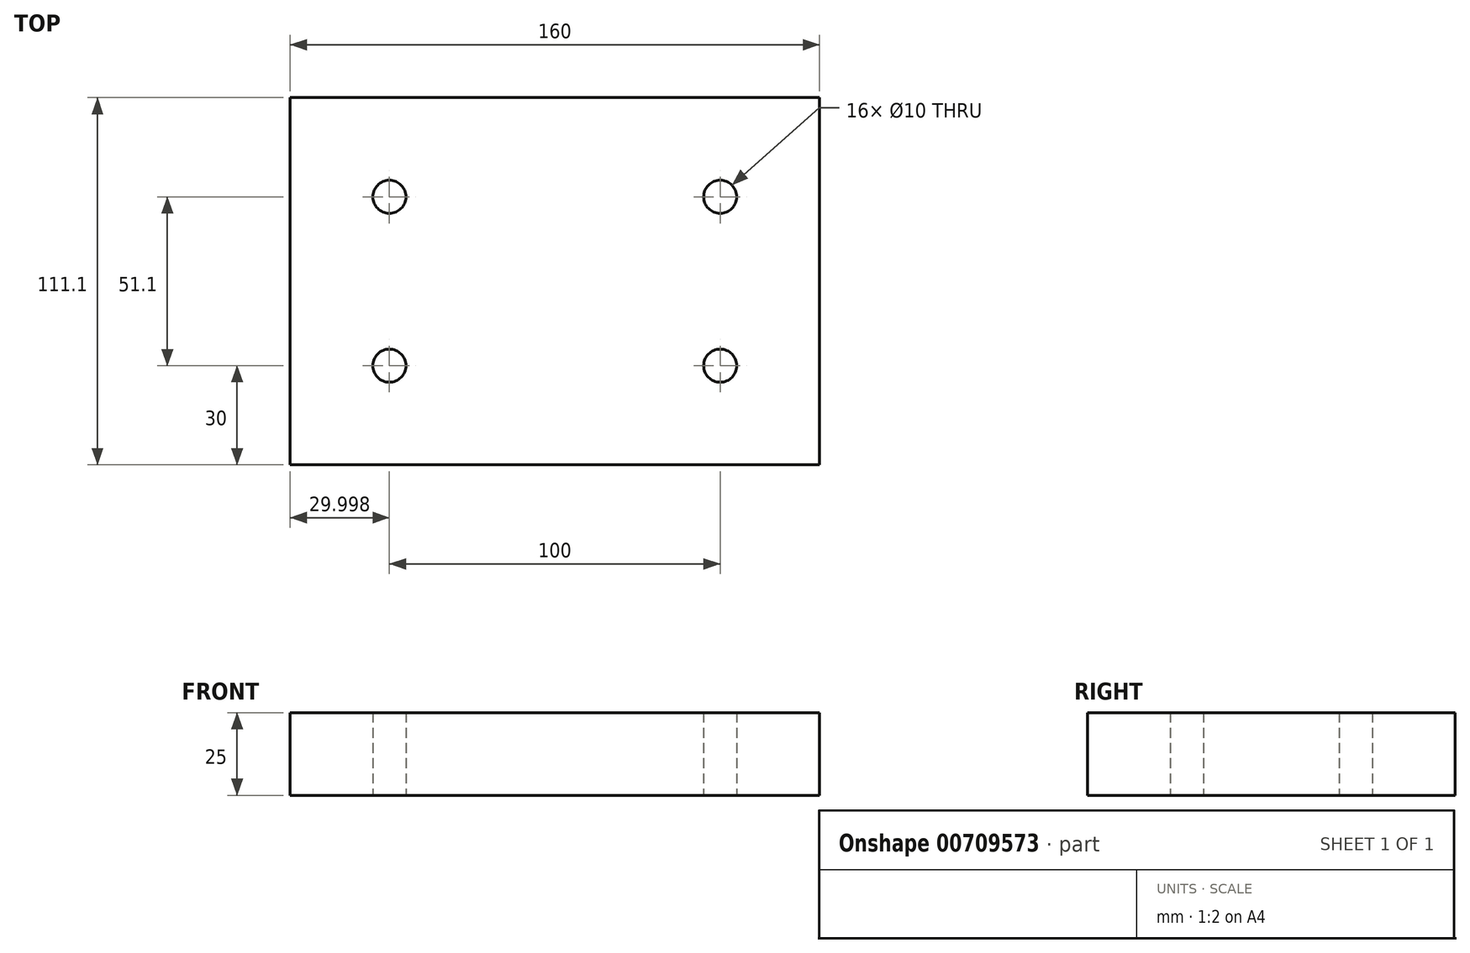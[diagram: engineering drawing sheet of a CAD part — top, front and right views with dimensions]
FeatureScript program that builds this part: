
annotation { "Feature Type Name" : "Feature", "Feature Type Description" : "" }
export const myFeature = defineFeature(function(context is Context, id is Id, definition is map)
    precondition{}
    {
        {
            var Q0;
            Q0=qCreatedBy(makeId("Top.planeOp"),FACE);
            var sketch = newSketch(context, id + "F0", { "sketchPlane" : qUnion([Q0])});
            skLineSegment(sketch, "E0.bottom", {"start": v(-87, 81.1) * mm, "end": v(73, 81.1) * mm});
            skLineSegment(sketch, "E0.top", {"start": v(-87, -30) * mm, "end": v(73, -30) * mm});
            skLineSegment(sketch, "E0.left", {"start": v(-87, 81.1) * mm, "end": v(-87, -30) * mm});
            skLineSegment(sketch, "E0.right", {"start": v(73, 81.1) * mm, "end": v(73, -30) * mm});
            skCircle(sketch, "E1", {"center": v(-57, 51.1) * mm, "radius": 5 * mm});
            skCircle(sketch, "E2", {"center": v(-57, 0) * mm, "radius": 5 * mm});
            skCircle(sketch, "E3", {"center": v(43, 51.1) * mm, "radius": 5 * mm});
            skCircle(sketch, "E4", {"center": v(43, 0) * mm, "radius": 5 * mm});
            skSolve(sketch);
        }
        {
            var Q0;
            Q0=makeQuery(id+"F0.imprint","IMPRINT",FACE,{"disambiguationData":[TD([[makeQuery(id+"F0.imprint","IMPRINT",EDGE,{"derivedFrom":sQuery(id+"F0.wireOp",EDGE,"E0.bottom")}),-1.0]])]});
            extrude(context, id + "F1", {"entities" : qUnion([Q0]), "depth" : 25 * mm, "offsetDistance" : 25 * mm});
        }
    });
